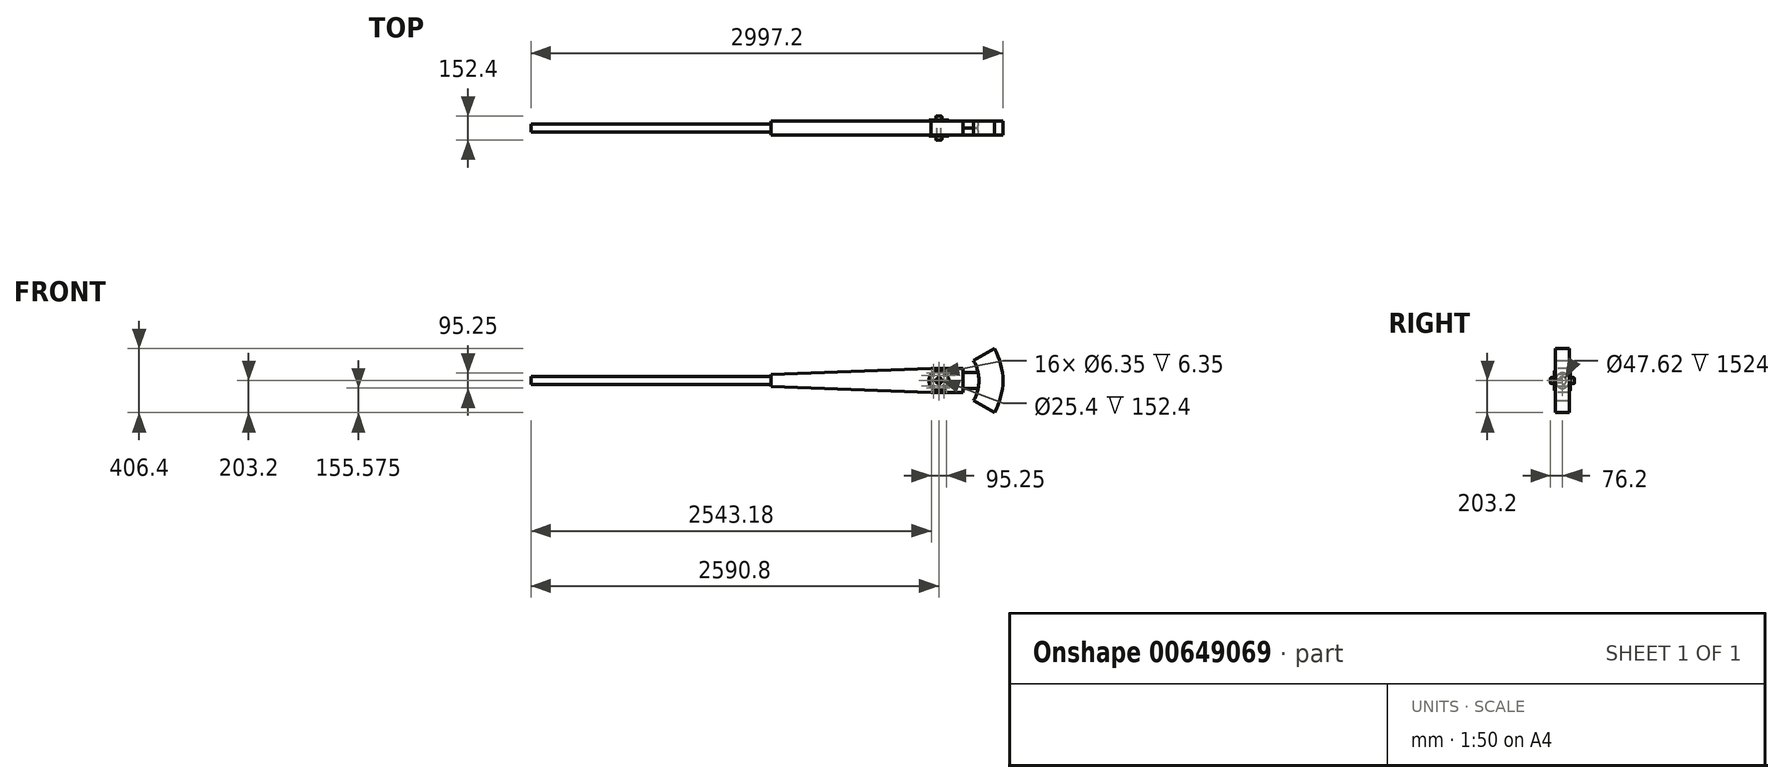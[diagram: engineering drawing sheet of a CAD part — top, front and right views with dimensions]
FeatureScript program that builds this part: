
annotation { "Feature Type Name" : "Feature", "Feature Type Description" : "" }
export const myFeature = defineFeature(function(context is Context, id is Id, definition is map)
    precondition{}
    {
        {
            var Q0;
            Q0=qCreatedBy(makeId("Front.planeOp"),FACE);
            var sketch = newSketch(context, id + "F0", { "sketchPlane" : qUnion([Q0])});
            skLineSegment(sketch, "E0", {"start": v(1066.8, 0) * mm, "end": v(-1371.6, 0) * mm, "construction": true});
            skLineSegment(sketch, "E1", {"start": v(-1371.6, 0) * mm, "end": v(-1371.6, 152.4) * mm, "construction": true});
            skLineSegment(sketch, "E2", {"start": v(-1371.6, 152.4) * mm, "end": v(1066.8, 152.4) * mm, "construction": true});
            skLineSegment(sketch, "E3", {"start": v(1066.8, 152.4) * mm, "end": v(1066.8, 0) * mm, "construction": true});
            skLineSegment(sketch, "E4", {"start": v(1066.8, 0) * mm, "end": v(1066.8, -152.4) * mm, "construction": true});
            skLineSegment(sketch, "E5", {"start": v(1066.8, -152.4) * mm, "end": v(-1371.6, -152.4) * mm, "construction": true});
            skLineSegment(sketch, "E6", {"start": v(-1371.6, 0) * mm, "end": v(-1371.6, -152.4) * mm, "construction": true});
            skCircle(sketch, "E7", {"center": v(1066.8, 0) * mm, "radius": 25.4 * mm, "construction": true});
            skSolve(sketch);
        }
        {
            var Q0;
            Q0=qCreatedBy(makeId("Front.planeOp"),FACE);
            var sketch = newSketch(context, id + "F1", { "sketchPlane" : qUnion([Q0])});
            skLineSegment(sketch, "E8.bottom", {"start": v(0, -76.2) * mm, "end": v(1219.2, -76.2) * mm});
            skLineSegment(sketch, "E8.top", {"start": v(0, 76.2) * mm, "end": v(1219.2, 76.2) * mm});
            skLineSegment(sketch, "E8.left", {"start": v(0, -76.2) * mm, "end": v(0, 76.2) * mm});
            skLineSegment(sketch, "E8.right", {"start": v(1219.2, -76.2) * mm, "end": v(1219.2, -50.8) * mm});
            skCircle(sketch, "E9", {"center": v(1066.8, 0) * mm, "radius": 12.7 * mm});
            skLineSegment(sketch, "E10.bottom", {"start": v(1219.2, -50.8) * mm, "end": v(1315.67, -50.8) * mm});
            skLineSegment(sketch, "E10.top", {"start": v(1219.2, 50.8) * mm, "end": v(1315.67, 50.8) * mm});
            skArc(sketch, "E11", {"start": v(1286.77, -127) * mm, "mid": v(1304.3, -90.07) * mm, "end": v(1315.67, -50.8) * mm});
            skArc(sketch, "E12", {"start": v(1418.75, -203.2) * mm, "mid": v(1473.2, 0) * mm, "end": v(1418.75, 203.2) * mm});
            skLineSegment(sketch, "E13", {"start": v(1418.75, 203.2) * mm, "end": v(1286.77, 127) * mm});
            skLineSegment(sketch, "E14.trimOffspring", {"start": v(1286.77, 127) * mm, "end": v(1418.75, 203.2) * mm});
            skLineSegment(sketch, "E15.trimOffspring", {"start": v(1286.77, -127) * mm, "end": v(1418.75, -203.2) * mm});
            skArc(sketch, "E16.trimOffspring", {"start": v(1315.67, 50.8) * mm, "mid": v(1304.3, 90.07) * mm, "end": v(1286.77, 127) * mm});
            skLineSegment(sketch, "E17.trimOffspring", {"start": v(1219.2, 50.8) * mm, "end": v(1219.2, 76.2) * mm});
            skSolve(sketch);
        }
        {
            var Q0;
            Q0=makeQuery(id+"F1.imprint","IMPRINT",FACE,{"disambiguationData":[TD([[makeQuery(id+"F1.imprint","IMPRINT",EDGE,{"derivedFrom":sQuery(id+"F1.wireOp",EDGE,"E8.bottom")}),1.0]])]});
            extrude(context, id + "F2", {"entities" : qUnion([Q0]), "depth" : 88.9 * mm, "offsetDistance" : 25.4 * mm});
        }
        {
            var Q0;
            Q0=makeQuery(id+"F2.opExtrude","CAP_FACE",FACE,{"disambiguationData":[OSD([sQuery(id+"F1.wireOp",EDGE,"E8.bottom"),sQuery(id+"F1.wireOp",EDGE,"E8.top"),sQuery(id+"F1.wireOp",EDGE,"E8.left"),sQuery(id+"F1.wireOp",EDGE,"E8.right"),sQuery(id+"F1.wireOp",EDGE,"E9")])],"isStart":false});
            var sketch = newSketch(context, id + "F3", { "sketchPlane" : qUnion([Q0])});
            skLineSegment(sketch, "E18", {"start": v(0, 76.2) * mm, "end": v(0, 38.1) * mm});
            skLineSegment(sketch, "E19", {"start": v(0, 38.1) * mm, "end": v(1016, 76.2) * mm});
            skLineSegment(sketch, "E20", {"start": v(1016, 76.2) * mm, "end": v(0, 76.2) * mm});
            skLineSegment(sketch, "E21", {"start": v(0, -76.2) * mm, "end": v(0, -38.1) * mm});
            skLineSegment(sketch, "E22", {"start": v(0, -38.1) * mm, "end": v(1016, -76.2) * mm});
            skLineSegment(sketch, "E23", {"start": v(1016, -76.2) * mm, "end": v(0, -76.2) * mm});
            skSolve(sketch);
        }
        {
            var Q0;
            Q0 = qSketchRegion(id + "F3", true);
            extrude(context, id + "F4", {"entities" : qUnion([Q0]), "operationType" : NewBodyOperationType.REMOVE, "oppositeDirection" : true, "depth" : 152.4 * mm, "offsetDistance" : 25.4 * mm});
        }
        {
            var Q0;
            Q0=makeQuery(id+"F2.opExtrude","SWEPT_FACE",FACE,{"disambiguationData":[OSD([sQuery(id+"F1.wireOp",EDGE,"E8.left")])]});
            var sketch = newSketch(context, id + "F5", { "sketchPlane" : qUnion([Q0])});
            skCircle(sketch, "E24", {"center": v(44.45, 0) * mm, "radius": 25.4 * mm});
            skCircle(sketch, "E25", {"center": v(44.45, 0) * mm, "radius": 23.81 * mm});
            skSolve(sketch);
        }
        {
            var Q0;
            Q0 = qSketchRegion(id + "F5", true);
            extrude(context, id + "F6", {"entities" : qUnion([Q0]), "operationType" : NewBodyOperationType.ADD, "depth" : 1524 * mm, "offsetDistance" : 25.4 * mm});
        }
        {
            var Q0;
            Q0=makeQuery(id+"F2.opExtrude","CAP_FACE",FACE,{"disambiguationData":[OSD([sQuery(id+"F1.wireOp",EDGE,"E8.bottom"),sQuery(id+"F1.wireOp",EDGE,"E8.top"),sQuery(id+"F1.wireOp",EDGE,"E8.left"),sQuery(id+"F1.wireOp",EDGE,"E8.right"),sQuery(id+"F1.wireOp",EDGE,"E9")])],"isStart":false});
            var sketch = newSketch(context, id + "F7", { "sketchPlane" : qUnion([Q0])});
            skCircle(sketch, "E26", {"center": v(1066.8, 0) * mm, "radius": 63.5 * mm});
            skCircle(sketch, "E27", {"center": v(1019.18, 0) * mm, "radius": 3.18 * mm});
            skCircle(sketch, "E28.1.1", {"center": v(1033.12, -33.68) * mm, "radius": 3.18 * mm});
            skCircle(sketch, "E28.2.1", {"center": v(1066.8, -47.63) * mm, "radius": 3.18 * mm});
            skCircle(sketch, "E28.3.1", {"center": v(1100.48, -33.68) * mm, "radius": 3.18 * mm});
            skCircle(sketch, "E28.4.1", {"center": v(1114.43, 0) * mm, "radius": 3.18 * mm});
            skCircle(sketch, "E28.5.1", {"center": v(1100.48, 33.68) * mm, "radius": 3.18 * mm});
            skCircle(sketch, "E28.6.1", {"center": v(1066.8, 47.63) * mm, "radius": 3.18 * mm});
            skCircle(sketch, "E28.7.1", {"center": v(1033.12, 33.68) * mm, "radius": 3.18 * mm});
            skCircle(sketch, "E29", {"center": v(1066.8, 0) * mm, "radius": 12.7 * mm});
            skSolve(sketch);
        }
        {
            var Q0;
            Q0 = qSketchRegion(id + "F7", true);
            extrude(context, id + "F8", {"entities" : qUnion([Q0]), "operationType" : NewBodyOperationType.ADD, "depth" : 6.35 * mm, "offsetDistance" : 25.4 * mm});
        }
        {
            var Q0;
            Q0=makeQuery(id+"F8.opExtrude","CAP_FACE",FACE,{"disambiguationData":[OSD([sQuery(id+"F7.wireOp",EDGE,"E27"),sQuery(id+"F7.wireOp",EDGE,"E28.1.1"),sQuery(id+"F7.wireOp",EDGE,"E28.2.1"),sQuery(id+"F7.wireOp",EDGE,"E28.3.1"),sQuery(id+"F7.wireOp",EDGE,"E28.4.1"),sQuery(id+"F7.wireOp",EDGE,"E28.5.1"),sQuery(id+"F7.wireOp",EDGE,"E28.6.1"),sQuery(id+"F7.wireOp",EDGE,"E26"),sQuery(id+"F7.wireOp",EDGE,"E28.7.1"),sQuery(id+"F7.wireOp",EDGE,"E29")])],"isStart":false});
            var sketch = newSketch(context, id + "F9", { "sketchPlane" : qUnion([Q0])});
            skCircle(sketch, "E30", {"center": v(1066.8, 0) * mm, "radius": 19.05 * mm});
            skCircle(sketch, "E31", {"center": v(1066.8, 0) * mm, "radius": 12.7 * mm});
            skSolve(sketch);
        }
        {
            var Q0;
            Q0 = qSketchRegion(id + "F9", true);
            extrude(context, id + "F10", {"entities" : qUnion([Q0]), "operationType" : NewBodyOperationType.ADD, "depth" : 25.4 * mm, "offsetDistance" : 25.4 * mm});
        }
        {
            var Q0;
            Q0=makeQuery(id+"F10.opExtrude","CAP_EDGE",EDGE,{"disambiguationData":[OSD([sQuery(id+"F9.wireOp",EDGE,"E30")])],"isStart":false});
            var Q1;
            Q1=makeQuery(id+"F8.opExtrude","CAP_EDGE",EDGE,{"disambiguationData":[OSD([sQuery(id+"F7.wireOp",EDGE,"E26")])],"isStart":false});
            fillet(context, id + "F11", {"entities" : qUnion([Q0, Q1]), "radius" : 5.08 * mm, "tangentPropagation" : true, "allowEdgeOverflow" : false});
        }
        {
            var Q0;
            Q0=makeQuery(id+"F2.opExtrude","CAP_FACE",FACE,{"disambiguationData":[OSD([sQuery(id+"F1.wireOp",EDGE,"E8.bottom"),sQuery(id+"F1.wireOp",EDGE,"E8.top"),sQuery(id+"F1.wireOp",EDGE,"E8.left"),sQuery(id+"F1.wireOp",EDGE,"E8.right"),sQuery(id+"F1.wireOp",EDGE,"E9")])],"isStart":true});
            var sketch = newSketch(context, id + "F12", { "sketchPlane" : qUnion([Q0])});
            skCircle(sketch, "E32", {"center": v(-1066.8, 0) * mm, "radius": 63.5 * mm});
            skCircle(sketch, "E33", {"center": v(-1066.8, 0) * mm, "radius": 12.7 * mm});
            skCircle(sketch, "E34", {"center": v(-1114.43, 0) * mm, "radius": 3.18 * mm});
            skCircle(sketch, "E35.1.0", {"center": v(-1100.48, -33.68) * mm, "radius": 3.18 * mm});
            skCircle(sketch, "E35.2.0", {"center": v(-1066.8, -47.63) * mm, "radius": 3.18 * mm});
            skCircle(sketch, "E35.3.0", {"center": v(-1033.12, -33.68) * mm, "radius": 3.18 * mm});
            skCircle(sketch, "E35.4.0", {"center": v(-1019.18, 0) * mm, "radius": 3.18 * mm});
            skCircle(sketch, "E35.5.0", {"center": v(-1033.12, 33.68) * mm, "radius": 3.18 * mm});
            skCircle(sketch, "E35.6.0", {"center": v(-1066.8, 47.63) * mm, "radius": 3.18 * mm});
            skCircle(sketch, "E35.7.0", {"center": v(-1100.48, 33.68) * mm, "radius": 3.18 * mm});
            skSolve(sketch);
        }
        {
            var Q0;
            Q0 = qSketchRegion(id + "F12", true);
            extrude(context, id + "F13", {"entities" : qUnion([Q0]), "operationType" : NewBodyOperationType.ADD, "depth" : 6.35 * mm, "offsetDistance" : 25.4 * mm});
        }
        {
            var Q0;
            Q0=makeQuery(id+"F13.opExtrude","CAP_FACE",FACE,{"disambiguationData":[OSD([sQuery(id+"F12.wireOp",EDGE,"E32"),sQuery(id+"F12.wireOp",EDGE,"E33"),sQuery(id+"F12.wireOp",EDGE,"E34"),sQuery(id+"F12.wireOp",EDGE,"E35.1.0"),sQuery(id+"F12.wireOp",EDGE,"E35.2.0"),sQuery(id+"F12.wireOp",EDGE,"E35.3.0"),sQuery(id+"F12.wireOp",EDGE,"E35.4.0"),sQuery(id+"F12.wireOp",EDGE,"E35.5.0"),sQuery(id+"F12.wireOp",EDGE,"E35.6.0"),sQuery(id+"F12.wireOp",EDGE,"E35.7.0")])],"isStart":false});
            var sketch = newSketch(context, id + "F14", { "sketchPlane" : qUnion([Q0])});
            skCircle(sketch, "E36", {"center": v(-1066.8, 0) * mm, "radius": 12.7 * mm});
            skCircle(sketch, "E37", {"center": v(-1066.8, 0) * mm, "radius": 19.05 * mm});
            skSolve(sketch);
        }
        {
            var Q0;
            Q0 = qSketchRegion(id + "F14", true);
            extrude(context, id + "F15", {"entities" : qUnion([Q0]), "operationType" : NewBodyOperationType.ADD, "depth" : 25.4 * mm, "offsetDistance" : 25.4 * mm});
        }
        {
            var Q0;
            Q0=makeQuery(id+"F13.opExtrude","CAP_EDGE",EDGE,{"disambiguationData":[OSD([sQuery(id+"F12.wireOp",EDGE,"E32")])],"isStart":false});
            var Q1;
            Q1=makeQuery(id+"F15.opExtrude","CAP_EDGE",EDGE,{"disambiguationData":[OSD([sQuery(id+"F14.wireOp",EDGE,"E37")])],"isStart":false});
            fillet(context, id + "F16", {"entities" : qUnion([Q0, Q1]), "radius" : 5.08 * mm, "tangentPropagation" : true, "allowEdgeOverflow" : false});
        }
        {
            var Q0;
            Q0=makeQuery(id+"F2.opExtrude","CAP_EDGE",EDGE,{"disambiguationData":[OSD([sQuery(id+"F1.wireOp",EDGE,"E10.top")])],"isStart":false});
            var Q1;
            Q1=makeQuery(id+"F2.opExtrude","CAP_EDGE",EDGE,{"disambiguationData":[OSD([sQuery(id+"F1.wireOp",EDGE,"E10.bottom")])],"isStart":false});
            var Q2;
            Q2=makeQuery(id+"F2.opExtrude","CAP_EDGE",EDGE,{"disambiguationData":[OSD([sQuery(id+"F1.wireOp",EDGE,"E10.bottom")])],"isStart":true});
            var Q3;
            Q3=makeQuery(id+"F2.opExtrude","CAP_EDGE",EDGE,{"disambiguationData":[OSD([sQuery(id+"F1.wireOp",EDGE,"E10.top")])],"isStart":true});
            fillet(context, id + "F17", {"entities" : qUnion([Q0, Q1, Q2, Q3]), "radius" : 50.55 * mm, "tangentPropagation" : true, "allowEdgeOverflow" : false});
        }
    });
